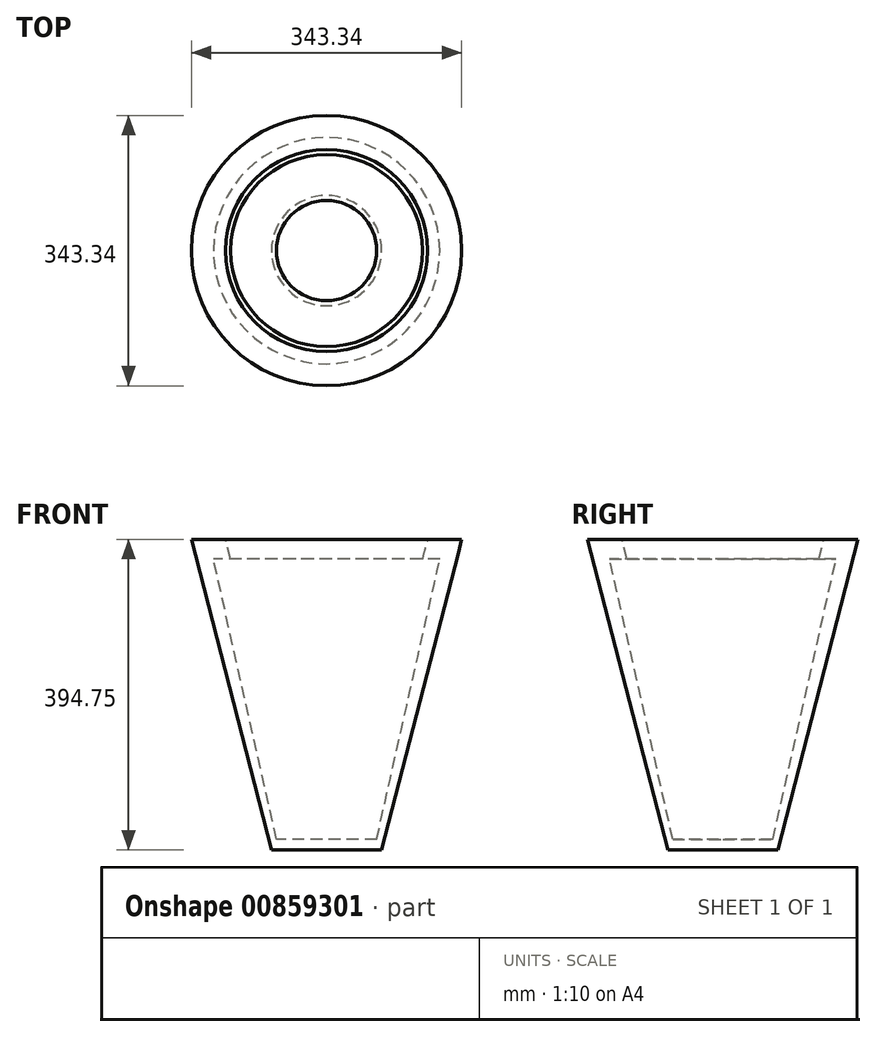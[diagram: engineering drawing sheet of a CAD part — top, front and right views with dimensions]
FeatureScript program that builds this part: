
annotation { "Feature Type Name" : "Feature", "Feature Type Description" : "" }
export const myFeature = defineFeature(function(context is Context, id is Id, definition is map)
    precondition{}
    {
        {
            var Q0;
            Q0=qCreatedBy(makeId("Front.planeOp"),FACE);
            var sketch = newSketch(context, id + "F0", { "sketchPlane" : qUnion([Q0])});
            skLineSegment(sketch, "E0", {"start": v(0, -215.35) * mm, "end": v(70, -215.35) * mm});
            skLineSegment(sketch, "E1", {"start": v(70, -215.35) * mm, "end": v(171.67, 179.4) * mm});
            skLineSegment(sketch, "E2", {"start": v(171.67, 179.4) * mm, "end": v(128.43, 179.4) * mm});
            skLineSegment(sketch, "E3", {"start": v(128.43, 179.4) * mm, "end": v(121.95, 154.24) * mm});
            skLineSegment(sketch, "E4", {"start": v(121.95, 154.24) * mm, "end": v(143.78, 154.24) * mm});
            skLineSegment(sketch, "E5", {"start": v(143.78, 154.24) * mm, "end": v(63.63, -201.73) * mm});
            skLineSegment(sketch, "E6", {"start": v(63.63, -201.73) * mm, "end": v(0, -201.73) * mm});
            skLineSegment(sketch, "E7", {"start": v(0, -201.73) * mm, "end": v(0, -215.35) * mm});
            skLineSegment(sketch, "E8", {"start": v(0, 117.09) * mm, "end": v(-3.8, 117.68) * mm});
            skSolve(sketch);
        }
        {
            var Q0;
            Q0=makeQuery(id+"F0.imprint","IMPRINT",FACE,{"disambiguationData":[TD([[makeQuery(id+"F0.imprint","IMPRINT",EDGE,{"derivedFrom":sQuery(id+"F0.wireOp",EDGE,"E0")}),1.0]])]});
            var Q1;
            Q1=sQuery(id+"F0.wireOp",EDGE,"E7");
            revolve(context, id + "F1", {"surfaceOperationType" : NewSurfaceOperationType.NEW, "entities" : qUnion([Q0]), "axis" : qUnion([Q1]), "revolveType" : RevolveType.FULL});
        }
    });
